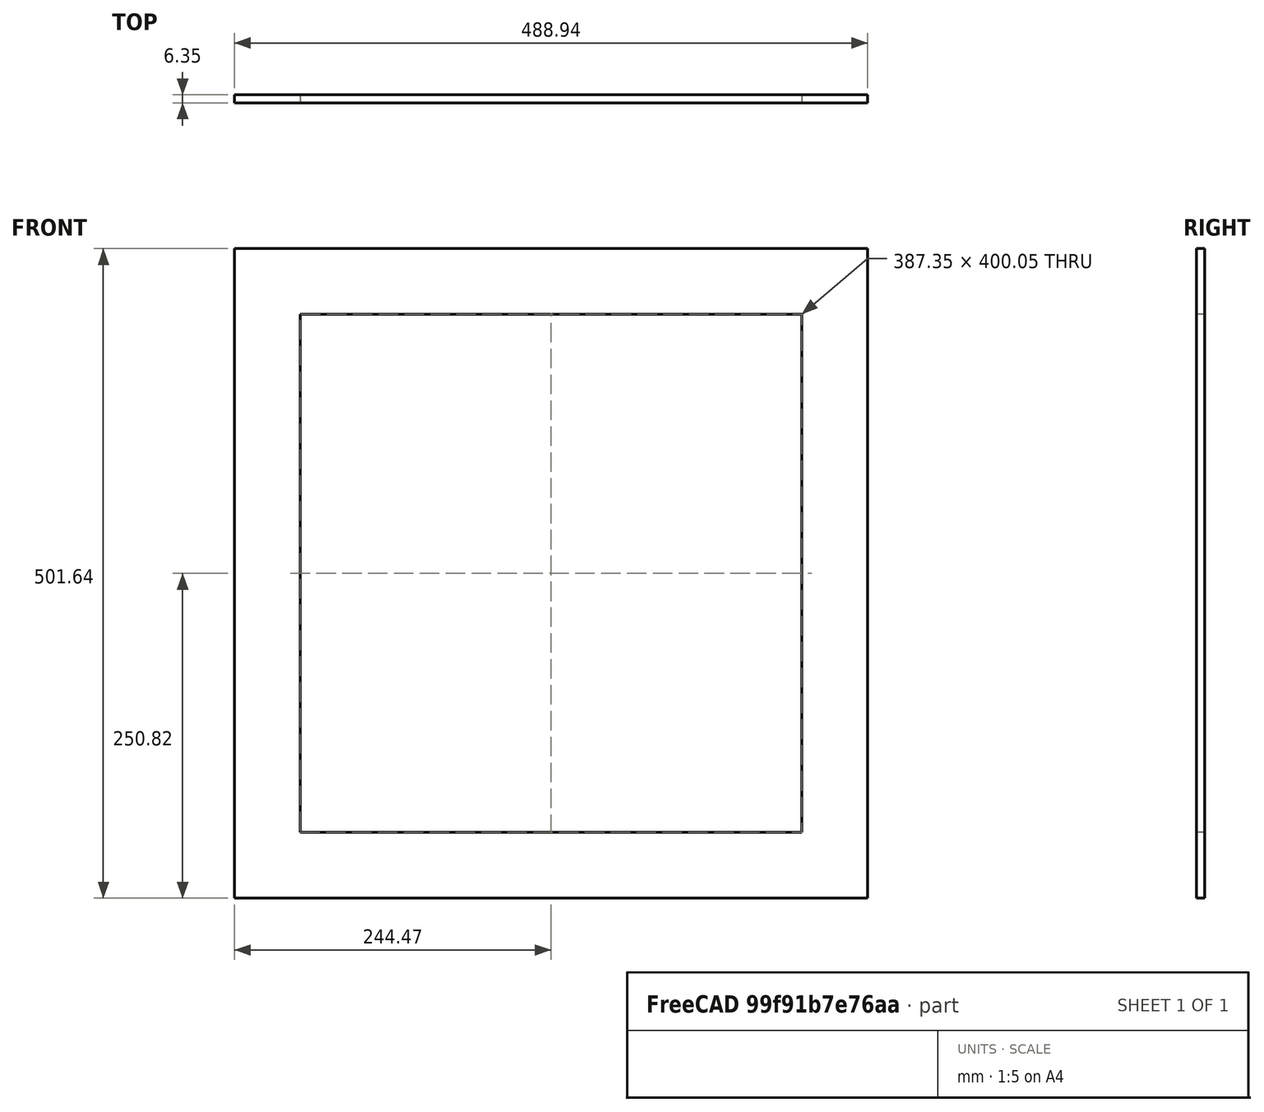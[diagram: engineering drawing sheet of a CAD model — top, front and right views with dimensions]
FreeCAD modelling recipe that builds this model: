
FCSTD DOCUMENT  (FreeCAD 0.16R6712 (Git))
Label: back
License: CreativeCommons Attribution-ShareAlike
LicenseURL: http://creativecommons.org/licenses/by-sa/4.0/
objects: Sketcher::SketchObject×1, PartDesign::Pad×1
note: 3 computed .brp shape members not serialized (recipe doc carries the construction recipe); baked Part::Feature solids carry a one-line shape summary decoded from their .brp

FEATURE [Sketcher::SketchObject] Sketch
  Placement = pos=(0,0,0) rot=(1,0,0;1.5708rad)
  sketch-geometry (10):
    g0: LineSegment StartX=-244.475 StartY=250.825 StartZ=0 EndX=244.475 EndY=250.825 EndZ=0
    g1: LineSegment StartX=244.475 StartY=250.825 StartZ=0 EndX=244.475 EndY=-250.825 EndZ=0
    g2: LineSegment StartX=244.475 StartY=-250.825 StartZ=0 EndX=-244.475 EndY=-250.825 EndZ=0
    g3: LineSegment StartX=-244.475 StartY=-250.825 StartZ=0 EndX=-244.475 EndY=250.825 EndZ=0
    g4: LineSegment StartX=-193.675 StartY=200.025 StartZ=0 EndX=193.675 EndY=200.025 EndZ=0
    g5: LineSegment StartX=193.675 StartY=200.025 StartZ=0 EndX=193.675 EndY=-200.025 EndZ=0
    g6: LineSegment StartX=193.675 StartY=-200.025 StartZ=0 EndX=-193.675 EndY=-200.025 EndZ=0
    g7: LineSegment StartX=-193.675 StartY=-200.025 StartZ=0 EndX=-193.675 EndY=200.025 EndZ=0
    g8: LineSegment [constr] StartX=-193.675 StartY=200.025 StartZ=0 EndX=-193.675 EndY=250.825 EndZ=0
    g9: LineSegment [constr] StartX=-193.675 StartY=200.025 StartZ=0 EndX=-244.475 EndY=200.025 EndZ=0
  constraints (32):
    c: Coincident(g0,g1)
    c: Coincident(g1,g2)
    c: Coincident(g2,g3)
    c: Coincident(g3,g0)
    c: Horizontal(g0)
    c: Horizontal(g2)
    c: Vertical(g1)
    c: Vertical(g3)
    c: Equal(g1,g3)
    c: Equal(g0,g2)
    c: Symmetric(g0,g2,g-1)
    c: DistanceX(g0,g0) = 488.95  'width'
    c: DistanceY(g1,g1) = 501.65
    c: Coincident(g4,g5)
    c: Coincident(g5,g6)
    c: Coincident(g6,g7)
    c: Coincident(g7,g4)
    c: Horizontal(g4)
    c: Horizontal(g6)
    c: Vertical(g5)
    c: Vertical(g7)
    c: Equal(g5,g7)
    c: Equal(g4,g6)
    c: Symmetric(g4,g5,g-1)
    c: Coincident(g8,g4)
    c: PointOnObject(g8,g0)
    c: Vertical(g8)
    c: Coincident(g9,g4)
    c: PointOnObject(g9,g3)
    c: Horizontal(g9)
    c: Equal(g8,g9)
    c: DistanceY(g8,g8) = 50.8
FEATURE [PartDesign::Pad] Pad
  Length = 6.35
  Length2 = 100
  Placement = pos=(0,0,0) rot=(1,0,0;1.5708rad)
  Sketch = -> Sketch
  Type = 0
